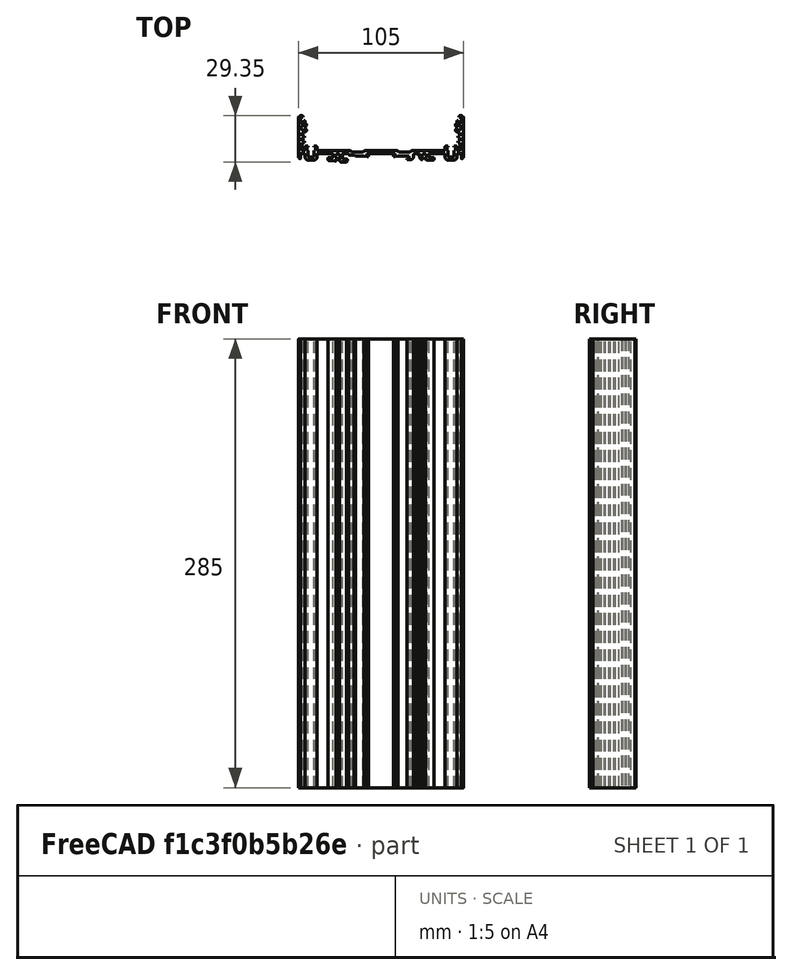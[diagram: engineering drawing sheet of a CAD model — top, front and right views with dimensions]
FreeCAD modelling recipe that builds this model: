
FCSTD DOCUMENT  (FreeCAD 0.20R29603 (Git))
Label: UM-ALU 4-100,5
License: All rights reserved
LicenseURL: http://en.wikipedia.org/wiki/All_rights_reserved
objects: Sketcher::SketchObject×1, PartDesign::Pad×1, PartDesign::Body×1
note: 4 computed .brp shape members not serialized (recipe doc carries the construction recipe); baked Part::Feature solids carry a one-line shape summary decoded from their .brp

FEATURE [Sketcher::SketchObject] Sketch
  FullyConstrained = false
  sketch-geometry (235):
    g0: LineSegment StartX=-40.7 StartY=5.3 StartZ=0 EndX=-40.7 EndY=4 EndZ=0
    g1: ArcOfCircle CenterX=-41.7 CenterY=5.3 CenterZ=0 NormalX=0 NormalY=0 NormalZ=1 AngleXU=1.5708 Radius=1 StartAngle=4.71239 EndAngle=6.28319
    g2: LineSegment StartX=-42.8 StartY=6.3 StartZ=0 EndX=-41.7 EndY=6.3 EndZ=0
    g3: LineSegment StartX=-42.8 StartY=5.6 StartZ=0 EndX=-42.8 EndY=6.3 EndZ=0
    g4: LineSegment StartX=-41.9 StartY=5.6 StartZ=0 EndX=-42.8 EndY=5.6 EndZ=0
    g5: LineSegment StartX=-41.9 StartY=3.4 StartZ=0 EndX=-41.9 EndY=5.6 EndZ=0
    g6: LineSegment StartX=-42.8 StartY=3.4 StartZ=0 EndX=-41.9 EndY=3.4 EndZ=0
    g7: LineSegment StartX=-42.8 StartY=-0.1 StartZ=0 EndX=-42.8 EndY=3.4 EndZ=0
    g8: ArcOfCircle CenterX=-43.3 CenterY=-0.1 CenterZ=0 NormalX=0 NormalY=0 NormalZ=1 AngleXU=1.5708 Radius=0.5 StartAngle=3.14159 EndAngle=4.71239
    g9: LineSegment StartX=-45.9 StartY=-0.6 StartZ=0 EndX=-43.3 EndY=-0.6 EndZ=0
    g10: ArcOfCircle CenterX=-45.9 CenterY=-0.1 CenterZ=0 NormalX=0 NormalY=0 NormalZ=1 AngleXU=1.5708 Radius=0.5 StartAngle=1.5708 EndAngle=3.14159
    g11: LineSegment StartX=-46.4 StartY=3.4 StartZ=0 EndX=-46.4 EndY=-0.1 EndZ=0
    g12: LineSegment StartX=-47.3 StartY=3.4 StartZ=0 EndX=-46.4 EndY=3.4 EndZ=0
    g13: LineSegment StartX=-47.3 StartY=5.6 StartZ=0 EndX=-47.3 EndY=3.4 EndZ=0
    g14: LineSegment StartX=-46.4 StartY=5.6 StartZ=0 EndX=-47.3 EndY=5.6 EndZ=0
    g15: LineSegment StartX=-46.4 StartY=6.3 StartZ=0 EndX=-46.4 EndY=5.6 EndZ=0
    g16: LineSegment StartX=-47.5 StartY=6.3 StartZ=0 EndX=-46.4 EndY=6.3 EndZ=0
    g17: ArcOfCircle CenterX=-47.5 CenterY=5.3 CenterZ=0 NormalX=0 NormalY=0 NormalZ=1 AngleXU=1.5708 Radius=1 StartAngle=0 EndAngle=1.5708
    g18: LineSegment StartX=-48.5 StartY=4 StartZ=0 EndX=-48.5 EndY=5.3 EndZ=0
    g19: ArcOfCircle CenterX=-49 CenterY=4 CenterZ=0 NormalX=0 NormalY=0 NormalZ=1 AngleXU=1.5708 Radius=0.5 StartAngle=3.14159 EndAngle=4.71239
    g20: LineSegment StartX=-50.1 StartY=3.5 StartZ=0 EndX=-49 EndY=3.5 EndZ=0
    g21: ArcOfCircle CenterX=-50.1 CenterY=3.8 CenterZ=0 NormalX=0 NormalY=0 NormalZ=1 AngleXU=1.5708 Radius=0.3 StartAngle=1.5708 EndAngle=3.14159
    g22: LineSegment StartX=-50.4 StartY=8.5 StartZ=0 EndX=-50.4 EndY=3.8 EndZ=0
    g23: LineSegment StartX=-48.9 StartY=8.5 StartZ=0 EndX=-50.4 EndY=8.5 EndZ=0
    g24: LineSegment StartX=-48.9 StartY=9.5 StartZ=0 EndX=-48.9 EndY=8.5 EndZ=0
    g25: LineSegment StartX=-50.4 StartY=9.5 StartZ=0 EndX=-48.9 EndY=9.5 EndZ=0
    g26: LineSegment StartX=-50.4 StartY=11.7 StartZ=0 EndX=-50.4 EndY=9.5 EndZ=0
    g27: LineSegment StartX=-48.9 StartY=11.7 StartZ=0 EndX=-50.4 EndY=11.7 EndZ=0
    g28: LineSegment StartX=-48.9 StartY=12.7 StartZ=0 EndX=-48.9 EndY=11.7 EndZ=0
    g29: LineSegment StartX=-50.4 StartY=12.7 StartZ=0 EndX=-48.9 EndY=12.7 EndZ=0
    g30: LineSegment StartX=-50.4 StartY=14.9 StartZ=0 EndX=-50.4 EndY=12.7 EndZ=0
    g31: LineSegment StartX=-49.65 StartY=14.9 StartZ=0 EndX=-50.4 EndY=14.9 EndZ=0
    g32: ArcOfCircle CenterX=-49.65 CenterY=17.9 CenterZ=0 NormalX=0 NormalY=0 NormalZ=1 AngleXU=1.5708 Radius=3 StartAngle=3.14159 EndAngle=3.97576
    g33: ArcOfCircle CenterX=-47.65 CenterY=16.0862 CenterZ=0 NormalX=0 NormalY=0 NormalZ=1 AngleXU=1.5708 Radius=0.3 StartAngle=3.97576 EndAngle=4.71239
    g34: LineSegment StartX=-47.35 StartY=16.3989 StartZ=0 EndX=-47.35 EndY=16.0862 EndZ=0
    g35: ArcOfCircle CenterX=-47.65 CenterY=16.3989 CenterZ=0 NormalX=0 NormalY=0 NormalZ=1 AngleXU=1.5708 Radius=0.3 StartAngle=4.71239 EndAngle=5.75959
    g36: LineSegment StartX=-48.2009 StartY=17.0633 StartZ=0 EndX=-47.5 EndY=16.6587 EndZ=0
    g37: ArcOfCircle CenterX=-48.3509 CenterY=16.8035 CenterZ=0 NormalX=0 NormalY=0 NormalZ=1 AngleXU=1.5708 Radius=0.3 StartAngle=5.75959 EndAngle=7.15298
    g38: ArcOfCircle CenterX=-49.65 CenterY=17.9 CenterZ=0 NormalX=0 NormalY=0 NormalZ=1 AngleXU=1.5708 Radius=1.4 StartAngle=5.41339 EndAngle=10.2946
    g39: ArcOfCircle CenterX=-48.3509 CenterY=18.9965 CenterZ=0 NormalX=0 NormalY=0 NormalZ=1 AngleXU=1.5708 Radius=0.3 StartAngle=2.27179 EndAngle=3.66519
    g40: LineSegment StartX=-47.5 StartY=19.1413 StartZ=0 EndX=-48.2009 EndY=18.7367 EndZ=0
    g41: ArcOfCircle CenterX=-47.65 CenterY=19.4011 CenterZ=0 NormalX=0 NormalY=0 NormalZ=1 AngleXU=1.5708 Radius=0.3 StartAngle=3.66519 EndAngle=4.71239
    g42: LineSegment StartX=-47.35 StartY=19.7138 StartZ=0 EndX=-47.35 EndY=19.4011 EndZ=0
    g43: ArcOfCircle CenterX=-47.65 CenterY=19.7138 CenterZ=0 NormalX=0 NormalY=0 NormalZ=1 AngleXU=1.5708 Radius=0.3 StartAngle=4.71239 EndAngle=5.44901
    g44: ArcOfCircle CenterX=-49.65 CenterY=17.9 CenterZ=0 NormalX=0 NormalY=0 NormalZ=1 AngleXU=1.5708 Radius=3 StartAngle=5.44901 EndAngle=5.777
    g45: ArcOfCircle CenterX=-48.05 CenterY=20.7862 CenterZ=0 NormalX=0 NormalY=0 NormalZ=1 AngleXU=1.5708 Radius=0.3 StartAngle=1.5708 EndAngle=2.6354
    g46: LineSegment StartX=-48.35 StartY=22 StartZ=0 EndX=-48.35 EndY=20.7862 EndZ=0
    g47: ArcOfCircle CenterX=-48.65 CenterY=22 CenterZ=0 NormalX=0 NormalY=0 NormalZ=1 AngleXU=1.5708 Radius=0.3 StartAngle=4.71239 EndAngle=6.28319
    g48: LineSegment StartX=-48.8851 StartY=22.3 StartZ=0 EndX=-48.65 EndY=22.3 EndZ=0
    g49: ArcOfCircle CenterX=-48.8851 CenterY=22 CenterZ=0 NormalX=0 NormalY=0 NormalZ=1 AngleXU=1.5708 Radius=0.3 StartAngle=0 EndAngle=1.80366
    g50: ArcOfCircle CenterX=-50.15 CenterY=21.7 CenterZ=0 NormalX=0 NormalY=0 NormalZ=1 AngleXU=1.5708 Radius=1 StartAngle=1.5708 EndAngle=4.94526
    g51: LineSegment StartX=-51.15 StartY=24.2 StartZ=0 EndX=-51.15 EndY=21.7 EndZ=0
    g52: ArcOfCircle CenterX=-50.85 CenterY=24.2 CenterZ=0 NormalX=0 NormalY=0 NormalZ=1 AngleXU=1.5708 Radius=0.3 StartAngle=0 EndAngle=1.5708
    g53: LineSegment StartX=-49.65 StartY=24.5 StartZ=0 EndX=-50.85 EndY=24.5 EndZ=0
    g54: LineSegment StartX=-49.65 StartY=25 StartZ=0 EndX=-49.65 EndY=24.5 EndZ=0
    g55: ArcOfCircle CenterX=-50.15 CenterY=25 CenterZ=0 NormalX=0 NormalY=0 NormalZ=1 AngleXU=1.5708 Radius=0.5 StartAngle=4.71239 EndAngle=6.28319
    g56: LineSegment StartX=-51.15 StartY=25.5 StartZ=0 EndX=-50.15 EndY=25.5 EndZ=0
    g57: ArcOfCircle CenterX=-51.15 CenterY=24.5 CenterZ=0 NormalX=0 NormalY=0 NormalZ=1 AngleXU=1.5708 Radius=1 StartAngle=0 EndAngle=1.09107
    g58: ArcOfCircle CenterX=-52.3033 CenterY=25.1 CenterZ=0 NormalX=0 NormalY=0 NormalZ=1 AngleXU=1.5708 Radius=0.3 StartAngle=3.14159 EndAngle=4.23266
    g59: LineSegment StartX=-52.35 StartY=24.8 StartZ=0 EndX=-52.3033 EndY=24.8 EndZ=0
    g60: ArcOfCircle CenterX=-52.35 CenterY=24.5 CenterZ=0 NormalX=0 NormalY=0 NormalZ=1 AngleXU=1.5708 Radius=0.3 StartAngle=0 EndAngle=1.5708
    g61: LineSegment StartX=-52.65 StartY=-0.205713 StartZ=0 EndX=-52.65 EndY=24.5 EndZ=0
    g62: ArcOfCircle CenterX=-50.85 CenterY=-0.205713 CenterZ=0 NormalX=0 NormalY=0 NormalZ=1 AngleXU=1.5708 Radius=1.8 StartAngle=1.5708 EndAngle=2.72258
    g63: LineSegment StartX=-51.45 StartY=-1.85 StartZ=0 EndX=-51.5823 EndY=-1.85 EndZ=0
    g64: ArcOfCircle CenterX=-51.45 CenterY=-1.55 CenterZ=0 NormalX=0 NormalY=0 NormalZ=1 AngleXU=1.5708 Radius=0.3 StartAngle=3.14159 EndAngle=4.71239
    g65: LineSegment StartX=-51.15 StartY=1.2 StartZ=0 EndX=-51.15 EndY=-1.55 EndZ=0
    g66: ArcOfCircle CenterX=-50.85 CenterY=1.2 CenterZ=0 NormalX=0 NormalY=0 NormalZ=1 AngleXU=1.5708 Radius=0.3 StartAngle=0 EndAngle=1.5708
    g67: LineSegment StartX=-48.9 StartY=1.5 StartZ=0 EndX=-50.85 EndY=1.5 EndZ=0
    g68: ArcOfCircle CenterX=-48.9 CenterY=1 CenterZ=0 NormalX=0 NormalY=0 NormalZ=1 AngleXU=1.5708 Radius=0.5 StartAngle=4.71239 EndAngle=6.28319
    g69: LineSegment StartX=-48.4 StartY=-0.6 StartZ=0 EndX=-48.4 EndY=1 EndZ=0
    g70: ArcOfCircle CenterX=-46.4 CenterY=-0.6 CenterZ=0 NormalX=0 NormalY=0 NormalZ=1 AngleXU=1.5708 Radius=2 StartAngle=1.5708 EndAngle=3.14159
    g71: LineSegment StartX=-42.8 StartY=-2.6 StartZ=0 EndX=-46.4 EndY=-2.6 EndZ=0
    g72: ArcOfCircle CenterX=-42.8 CenterY=-0.6 CenterZ=0 NormalX=0 NormalY=0 NormalZ=1 AngleXU=1.5708 Radius=2 StartAngle=3.14159 EndAngle=4.71239
    g73: LineSegment StartX=-40.8 StartY=1 StartZ=0 EndX=-40.8 EndY=-0.6 EndZ=0
    g74: ArcOfCircle CenterX=-40.3 CenterY=1 CenterZ=0 NormalX=0 NormalY=0 NormalZ=1 AngleXU=1.5708 Radius=0.5 StartAngle=0 EndAngle=1.5708
    g75: LineSegment StartX=-30.95 StartY=1.5 StartZ=0 EndX=-40.3 EndY=1.5 EndZ=0
    g76: ArcOfCircle CenterX=-30.95 CenterY=1.2 CenterZ=0 NormalX=0 NormalY=0 NormalZ=1 AngleXU=1.5708 Radius=0.3 StartAngle=4.71239 EndAngle=6.28319
    g77: LineSegment StartX=-30.65 StartY=-0.85 StartZ=0 EndX=-30.65 EndY=1.2 EndZ=0
    g78: ArcOfCircle CenterX=-30.95 CenterY=-0.85 CenterZ=0 NormalX=0 NormalY=0 NormalZ=1 AngleXU=1.5708 Radius=0.3 StartAngle=3.14159 EndAngle=4.71239
    g79: LineSegment StartX=-33.55 StartY=-1.15 StartZ=0 EndX=-30.95 EndY=-1.15 EndZ=0
    g80: ArcOfCircle CenterX=-33.55 CenterY=-1.45 CenterZ=0 NormalX=0 NormalY=0 NormalZ=1 AngleXU=1.5708 Radius=0.3 StartAngle=0 EndAngle=1.5708
    g81: LineSegment StartX=-33.85 StartY=-2.37492 StartZ=0 EndX=-33.85 EndY=-1.45 EndZ=0
    g82: ArcOfCircle CenterX=-33.35 CenterY=-2.37492 CenterZ=0 NormalX=0 NormalY=0 NormalZ=1 AngleXU=1.5708 Radius=0.5 StartAngle=1.5708 EndAngle=3.01069
    g83: LineSegment StartX=-29.3653 StartY=-3.40384 StartZ=0 EndX=-33.4153 EndY=-2.87064 EndZ=0
    g84: ArcOfCircle CenterX=-29.3 CenterY=-2.90811 CenterZ=0 NormalX=0 NormalY=0 NormalZ=1 AngleXU=1.5708 Radius=0.5 StartAngle=3.01069 EndAngle=4.71239
    g85: LineSegment StartX=-28.8 StartY=-2.09186 StartZ=0 EndX=-28.8 EndY=-2.90811 EndZ=0
    g86: LineSegment StartX=-28.4867 StartY=-1.54914 StartZ=0 EndX=-28.8 EndY=-2.09186 EndZ=0
    g87: ArcOfCircle CenterX=-28.7465 CenterY=-1.39914 CenterZ=0 NormalX=0 NormalY=0 NormalZ=1 AngleXU=1.5708 Radius=0.3 StartAngle=4.18879 EndAngle=5.58219
    g88: ArcOfCircle CenterX=-27.65 CenterY=-0.1 CenterZ=0 NormalX=0 NormalY=0 NormalZ=1 AngleXU=1.5708 Radius=1.4 StartAngle=3.84259 EndAngle=8.72378
    g89: ArcOfCircle CenterX=-26.5535 CenterY=-1.39914 CenterZ=0 NormalX=0 NormalY=0 NormalZ=1 AngleXU=1.5708 Radius=0.3 StartAngle=0.700998 EndAngle=2.0944
    g90: LineSegment StartX=-26.5 StartY=-2.09186 StartZ=0 EndX=-26.8133 EndY=-1.54914 EndZ=0
    g91: LineSegment StartX=-26.5 StartY=-2.85 StartZ=0 EndX=-26.5 EndY=-2.09186 EndZ=0
    g92: ArcOfCircle CenterX=-25.5 CenterY=-2.85 CenterZ=0 NormalX=0 NormalY=0 NormalZ=1 AngleXU=1.5708 Radius=1 StartAngle=1.5708 EndAngle=3.14159
    g93: LineSegment StartX=-22.0274 StartY=-3.85 StartZ=0 EndX=-25.5 EndY=-3.85 EndZ=0
    g94: LineSegment StartX=-21.45 StartY=-2.85 StartZ=0 EndX=-22.0274 EndY=-3.85 EndZ=0
    g95: LineSegment StartX=-21.45 StartY=-2.45 StartZ=0 EndX=-21.45 EndY=-2.85 EndZ=0
    g96: ArcOfCircle CenterX=-21.75 CenterY=-2.45 CenterZ=0 NormalX=0 NormalY=0 NormalZ=1 AngleXU=1.5708 Radius=0.3 StartAngle=4.71239 EndAngle=6.28319
    g97: LineSegment StartX=-24.35 StartY=-2.15 StartZ=0 EndX=-21.75 EndY=-2.15 EndZ=0
    g98: ArcOfCircle CenterX=-24.35 CenterY=-1.85 CenterZ=0 NormalX=0 NormalY=0 NormalZ=1 AngleXU=1.5708 Radius=0.3 StartAngle=1.5708 EndAngle=3.14159
    g99: LineSegment StartX=-24.65 StartY=1.2 StartZ=0 EndX=-24.65 EndY=-1.85 EndZ=0
    g100: ArcOfCircle CenterX=-24.35 CenterY=1.2 CenterZ=0 NormalX=0 NormalY=0 NormalZ=1 AngleXU=1.5708 Radius=0.3 StartAngle=0 EndAngle=1.5708
    g101: LineSegment StartX=-20.95 StartY=1.5 StartZ=0 EndX=-24.35 EndY=1.5 EndZ=0
    g102: ArcOfCircle CenterX=-20.95 CenterY=1.2 CenterZ=0 NormalX=0 NormalY=0 NormalZ=1 AngleXU=1.5708 Radius=0.3 StartAngle=4.71239 EndAngle=6.28319
    g103: LineSegment StartX=-20.65 StartY=0.8 StartZ=0 EndX=-20.65 EndY=1.2 EndZ=0
    g104: ArcOfCircle CenterX=-20.35 CenterY=0.8 CenterZ=0 NormalX=0 NormalY=0 NormalZ=1 AngleXU=1.5708 Radius=0.3 StartAngle=1.5708 EndAngle=3.14159
    g105: LineSegment StartX=-17.216 StartY=0.5 StartZ=0 EndX=-20.35 EndY=0.5 EndZ=0
    g106: LineSegment StartX=-16.35 StartY=3.6e-15 StartZ=0 EndX=-17.216 EndY=0.5 EndZ=0
    g107: LineSegment StartX=-11.016 StartY=1.8e-15 StartZ=0 EndX=-16.35 EndY=3e-15 EndZ=0
    g108: LineSegment StartX=-9.15 StartY=-0.5 StartZ=0 EndX=-11.016 EndY=-3.13e-14 EndZ=0
    g109: LineSegment StartX=-8.15 StartY=-0.5 StartZ=0 EndX=-9.15 EndY=-0.5 EndZ=0
    g110: LineSegment StartX=-8.15 StartY=0.5 StartZ=0 EndX=-8.15 EndY=-0.5 EndZ=0
    g111: LineSegment StartX=-9.15 StartY=0.5 StartZ=0 EndX=-8.15 EndY=0.5 EndZ=0
    g112: LineSegment StartX=-9.15 StartY=1.5 StartZ=0 EndX=-9.15 EndY=0.5 EndZ=0
    g113: LineSegment StartX=8.85 StartY=1.5 StartZ=0 EndX=-9.15 EndY=1.5 EndZ=0
    g114: LineSegment StartX=8.85 StartY=0.5 StartZ=0 EndX=8.85 EndY=1.5 EndZ=0
    g115: LineSegment StartX=7.85 StartY=0.5 StartZ=0 EndX=8.85 EndY=0.5 EndZ=0
    g116: LineSegment StartX=7.85 StartY=-0.5 StartZ=0 EndX=7.85 EndY=0.5 EndZ=0
    g117: LineSegment StartX=8.85 StartY=-0.5 StartZ=0 EndX=7.85 EndY=-0.5 EndZ=0
    g118: LineSegment StartX=10.716 StartY=-1.8e-15 StartZ=0 EndX=8.85 EndY=-0.5 EndZ=0
    g119: LineSegment StartX=17.5 StartY=-3.6e-15 StartZ=0 EndX=10.716 EndY=-2e-15 EndZ=0
    g120: LineSegment StartX=17.5 StartY=-1.1 StartZ=0 EndX=17.5 EndY=-3.6e-15 EndZ=0
    g121: LineSegment StartX=16.3 StartY=-1.59706 StartZ=0 EndX=17.5 EndY=-1.1 EndZ=0
    g122: LineSegment StartX=16.3 StartY=-2.4 StartZ=0 EndX=16.3 EndY=-1.59706 EndZ=0
    g123: LineSegment StartX=18.5 StartY=-2.4 StartZ=0 EndX=16.3 EndY=-2.4 EndZ=0
    g124: ArcOfCircle CenterX=18.5 CenterY=-0.4 CenterZ=0 NormalX=0 NormalY=0 NormalZ=1 AngleXU=1.5708 Radius=2 StartAngle=3.14159 EndAngle=4.71239
    g125: LineSegment StartX=20.5 StartY=0.5 StartZ=0 EndX=20.5 EndY=-0.4 EndZ=0
    g126: ArcOfCircle CenterX=21.5 CenterY=0.5 CenterZ=0 NormalX=0 NormalY=0 NormalZ=1 AngleXU=1.5708 Radius=1 StartAngle=0 EndAngle=1.5708
    g127: LineSegment StartX=22.475 StartY=1.5 StartZ=0 EndX=21.5 EndY=1.5 EndZ=0
    g128: ArcOfCircle CenterX=22.775 CenterY=1.5 CenterZ=0 NormalX=0 NormalY=0 NormalZ=1 AngleXU=1.5708 Radius=0.3 StartAngle=1.5708 EndAngle=4.71239
    g129: LineSegment StartX=24.05 StartY=1.5 StartZ=0 EndX=23.075 EndY=1.5 EndZ=0
    g130: ArcOfCircle CenterX=24.05 CenterY=1.2 CenterZ=0 NormalX=0 NormalY=0 NormalZ=1 AngleXU=1.5708 Radius=0.3 StartAngle=4.71239 EndAngle=6.28319
    g131: LineSegment StartX=24.35 StartY=-0.1 StartZ=0 EndX=24.35 EndY=1.2 EndZ=0
    g132: ArcOfCircle CenterX=27.35 CenterY=-0.1 CenterZ=0 NormalX=0 NormalY=0 NormalZ=1 AngleXU=1.5708 Radius=3 StartAngle=1.5708 EndAngle=2.41664
    g133: ArcOfCircle CenterX=25.6922 CenterY=-1.97132 CenterZ=0 NormalX=0 NormalY=0 NormalZ=1 AngleXU=1.5708 Radius=0.5 StartAngle=2.41664 EndAngle=4.18879
    g134: LineSegment StartX=26.5133 StartY=-1.54914 StartZ=0 EndX=26.1253 EndY=-2.22132 EndZ=0
    g135: ArcOfCircle CenterX=26.2535 CenterY=-1.39914 CenterZ=0 NormalX=0 NormalY=0 NormalZ=1 AngleXU=1.5708 Radius=0.3 StartAngle=4.18879 EndAngle=5.58219
    g136: ArcOfCircle CenterX=27.35 CenterY=-0.1 CenterZ=0 NormalX=0 NormalY=0 NormalZ=1 AngleXU=1.5708 Radius=1.4 StartAngle=3.84259 EndAngle=8.72378
    g137: ArcOfCircle CenterX=28.4465 CenterY=-1.39914 CenterZ=0 NormalX=0 NormalY=0 NormalZ=1 AngleXU=1.5708 Radius=0.3 StartAngle=0.700998 EndAngle=2.0944
    g138: LineSegment StartX=28.7356 StartY=-2.5 StartZ=0 EndX=28.1867 EndY=-1.54914 EndZ=0
    g139: ArcOfCircle CenterX=28.9954 CenterY=-2.35 CenterZ=0 NormalX=0 NormalY=0 NormalZ=1 AngleXU=1.5708 Radius=0.3 StartAngle=2.0944 EndAngle=3.14159
    g140: LineSegment StartX=33.25 StartY=-2.65 StartZ=0 EndX=28.9954 EndY=-2.65 EndZ=0
    g141: ArcOfCircle CenterX=33.25 CenterY=-2.35 CenterZ=0 NormalX=0 NormalY=0 NormalZ=1 AngleXU=1.5708 Radius=0.3 StartAngle=3.14159 EndAngle=4.71239
    g142: LineSegment StartX=33.55 StartY=-1.45 StartZ=0 EndX=33.55 EndY=-2.35 EndZ=0
    g143: ArcOfCircle CenterX=33.25 CenterY=-1.45 CenterZ=0 NormalX=0 NormalY=0 NormalZ=1 AngleXU=1.5708 Radius=0.3 StartAngle=4.71239 EndAngle=6.28319
    g144: LineSegment StartX=30.65 StartY=-1.15 StartZ=0 EndX=33.25 EndY=-1.15 EndZ=0
    g145: ArcOfCircle CenterX=30.65 CenterY=-0.85 CenterZ=0 NormalX=0 NormalY=0 NormalZ=1 AngleXU=1.5708 Radius=0.3 StartAngle=1.5708 EndAngle=3.14159
    g146: LineSegment StartX=30.35 StartY=1.2 StartZ=0 EndX=30.35 EndY=-0.85 EndZ=0
    g147: ArcOfCircle CenterX=30.65 CenterY=1.2 CenterZ=0 NormalX=0 NormalY=0 NormalZ=1 AngleXU=1.5708 Radius=0.3 StartAngle=0 EndAngle=1.5708
    g148: LineSegment StartX=40 StartY=1.5 StartZ=0 EndX=30.65 EndY=1.5 EndZ=0
    g149: ArcOfCircle CenterX=40 CenterY=1 CenterZ=0 NormalX=0 NormalY=0 NormalZ=1 AngleXU=1.5708 Radius=0.5 StartAngle=4.71239 EndAngle=6.28319
    g150: LineSegment StartX=40.5 StartY=-0.6 StartZ=0 EndX=40.5 EndY=1 EndZ=0
    g151: ArcOfCircle CenterX=42.5 CenterY=-0.6 CenterZ=0 NormalX=0 NormalY=0 NormalZ=1 AngleXU=1.5708 Radius=2 StartAngle=1.5708 EndAngle=3.14159
    g152: LineSegment StartX=46.1 StartY=-2.6 StartZ=0 EndX=42.5 EndY=-2.6 EndZ=0
    g153: ArcOfCircle CenterX=46.1 CenterY=-0.6 CenterZ=0 NormalX=0 NormalY=0 NormalZ=1 AngleXU=1.5708 Radius=2 StartAngle=3.14159 EndAngle=4.71239
    g154: LineSegment StartX=48.1 StartY=1 StartZ=0 EndX=48.1 EndY=-0.6 EndZ=0
    g155: ArcOfCircle CenterX=48.6 CenterY=1 CenterZ=0 NormalX=0 NormalY=0 NormalZ=1 AngleXU=1.5708 Radius=0.5 StartAngle=0 EndAngle=1.5708
    g156: LineSegment StartX=50.55 StartY=1.5 StartZ=0 EndX=48.6 EndY=1.5 EndZ=0
    g157: ArcOfCircle CenterX=50.55 CenterY=1.2 CenterZ=0 NormalX=0 NormalY=0 NormalZ=1 AngleXU=1.5708 Radius=0.3 StartAngle=4.71239 EndAngle=6.28319
    g158: LineSegment StartX=50.85 StartY=-1.55 StartZ=0 EndX=50.85 EndY=1.2 EndZ=0
    g159: ArcOfCircle CenterX=51.15 CenterY=-1.55 CenterZ=0 NormalX=0 NormalY=0 NormalZ=1 AngleXU=1.5708 Radius=0.3 StartAngle=1.5708 EndAngle=3.14159
    g160: LineSegment StartX=51.2823 StartY=-1.85 StartZ=0 EndX=51.15 EndY=-1.85 EndZ=0
    g161: ArcOfCircle CenterX=50.55 CenterY=-0.205713 CenterZ=0 NormalX=0 NormalY=0 NormalZ=1 AngleXU=1.5708 Radius=1.8 StartAngle=3.5606 EndAngle=4.71239
    g162: LineSegment StartX=52.35 StartY=24.5 StartZ=0 EndX=52.35 EndY=-0.205713 EndZ=0
    g163: ArcOfCircle CenterX=52.05 CenterY=24.5 CenterZ=0 NormalX=0 NormalY=0 NormalZ=1 AngleXU=1.5708 Radius=0.3 StartAngle=4.71239 EndAngle=6.28319
    g164: LineSegment StartX=52.0033 StartY=24.8 StartZ=0 EndX=52.05 EndY=24.8 EndZ=0
    g165: ArcOfCircle CenterX=52.0033 CenterY=25.1 CenterZ=0 NormalX=0 NormalY=0 NormalZ=1 AngleXU=1.5708 Radius=0.3 StartAngle=2.05052 EndAngle=3.14159
    g166: ArcOfCircle CenterX=50.85 CenterY=24.5 CenterZ=0 NormalX=0 NormalY=0 NormalZ=1 AngleXU=1.5708 Radius=1 StartAngle=5.19212 EndAngle=6.28319
    g167: LineSegment StartX=49.85 StartY=25.5 StartZ=0 EndX=50.85 EndY=25.5 EndZ=0
    g168: ArcOfCircle CenterX=49.85 CenterY=25 CenterZ=0 NormalX=0 NormalY=0 NormalZ=1 AngleXU=1.5708 Radius=0.5 StartAngle=0 EndAngle=1.5708
    g169: LineSegment StartX=49.35 StartY=24.5 StartZ=0 EndX=49.35 EndY=25 EndZ=0
    g170: LineSegment StartX=50.55 StartY=24.5 StartZ=0 EndX=49.35 EndY=24.5 EndZ=0
    g171: ArcOfCircle CenterX=50.55 CenterY=24.2 CenterZ=0 NormalX=0 NormalY=0 NormalZ=1 AngleXU=1.5708 Radius=0.3 StartAngle=4.71239 EndAngle=6.28319
    g172: LineSegment StartX=50.85 StartY=21.7 StartZ=0 EndX=50.85 EndY=24.2 EndZ=0
    g173: ArcOfCircle CenterX=49.85 CenterY=21.7 CenterZ=0 NormalX=0 NormalY=0 NormalZ=1 AngleXU=1.5708 Radius=1 StartAngle=1.33793 EndAngle=4.71239
    g174: ArcOfCircle CenterX=48.5851 CenterY=22 CenterZ=0 NormalX=0 NormalY=0 NormalZ=1 AngleXU=1.5708 Radius=0.3 StartAngle=4.47952 EndAngle=6.28319
    g175: LineSegment StartX=48.35 StartY=22.3 StartZ=0 EndX=48.5851 EndY=22.3 EndZ=0
    g176: ArcOfCircle CenterX=48.35 CenterY=22 CenterZ=0 NormalX=0 NormalY=0 NormalZ=1 AngleXU=1.5708 Radius=0.3 StartAngle=0 EndAngle=1.5708
    g177: LineSegment StartX=48.05 StartY=20.7862 StartZ=0 EndX=48.05 EndY=22 EndZ=0
    g178: ArcOfCircle CenterX=47.75 CenterY=20.7862 CenterZ=0 NormalX=0 NormalY=0 NormalZ=1 AngleXU=1.5708 Radius=0.3 StartAngle=3.64778 EndAngle=4.71239
    g179: ArcOfCircle CenterX=49.35 CenterY=17.9 CenterZ=0 NormalX=0 NormalY=0 NormalZ=1 AngleXU=1.5708 Radius=3 StartAngle=0.50619 EndAngle=0.834172
    g180: ArcOfCircle CenterX=47.35 CenterY=19.7138 CenterZ=0 NormalX=0 NormalY=0 NormalZ=1 AngleXU=1.5708 Radius=0.3 StartAngle=0.834172 EndAngle=1.5708
    g181: LineSegment StartX=47.05 StartY=19.4011 StartZ=0 EndX=47.05 EndY=19.7138 EndZ=0
    g182: ArcOfCircle CenterX=47.35 CenterY=19.4011 CenterZ=0 NormalX=0 NormalY=0 NormalZ=1 AngleXU=1.5708 Radius=0.3 StartAngle=1.5708 EndAngle=2.61799
    g183: LineSegment StartX=47.9009 StartY=18.7367 StartZ=0 EndX=47.2 EndY=19.1413 EndZ=0
    g184: ArcOfCircle CenterX=48.0509 CenterY=18.9965 CenterZ=0 NormalX=0 NormalY=0 NormalZ=1 AngleXU=1.5708 Radius=0.3 StartAngle=2.61799 EndAngle=4.01139
    g185: ArcOfCircle CenterX=49.35 CenterY=17.9 CenterZ=0 NormalX=0 NormalY=0 NormalZ=1 AngleXU=1.5708 Radius=1.4 StartAngle=2.27179 EndAngle=7.15298
    g186: ArcOfCircle CenterX=48.0509 CenterY=16.8035 CenterZ=0 NormalX=0 NormalY=0 NormalZ=1 AngleXU=1.5708 Radius=0.3 StartAngle=5.41339 EndAngle=6.80678
    g187: LineSegment StartX=47.2 StartY=16.6587 StartZ=0 EndX=47.9009 EndY=17.0633 EndZ=0
    g188: ArcOfCircle CenterX=47.35 CenterY=16.3989 CenterZ=0 NormalX=0 NormalY=0 NormalZ=1 AngleXU=1.5708 Radius=0.3 StartAngle=0.523599 EndAngle=1.5708
    g189: LineSegment StartX=47.05 StartY=16.0862 StartZ=0 EndX=47.05 EndY=16.3989 EndZ=0
    g190: ArcOfCircle CenterX=47.35 CenterY=16.0862 CenterZ=0 NormalX=0 NormalY=0 NormalZ=1 AngleXU=1.5708 Radius=0.3 StartAngle=1.5708 EndAngle=2.30742
    g191: ArcOfCircle CenterX=49.35 CenterY=17.9 CenterZ=0 NormalX=0 NormalY=0 NormalZ=1 AngleXU=1.5708 Radius=3 StartAngle=2.30742 EndAngle=3.14159
    g192: LineSegment StartX=50.1 StartY=14.9 StartZ=0 EndX=49.35 EndY=14.9 EndZ=0
    g193: LineSegment StartX=50.1 StartY=12.7 StartZ=0 EndX=50.1 EndY=14.9 EndZ=0
    g194: LineSegment StartX=48.6 StartY=12.7 StartZ=0 EndX=50.1 EndY=12.7 EndZ=0
    g195: LineSegment StartX=48.6 StartY=11.7 StartZ=0 EndX=48.6 EndY=12.7 EndZ=0
    g196: LineSegment StartX=50.1 StartY=11.7 StartZ=0 EndX=48.6 EndY=11.7 EndZ=0
    g197: LineSegment StartX=50.1 StartY=9.5 StartZ=0 EndX=50.1 EndY=11.7 EndZ=0
    g198: LineSegment StartX=48.6 StartY=9.5 StartZ=0 EndX=50.1 EndY=9.5 EndZ=0
    g199: LineSegment StartX=48.6 StartY=8.5 StartZ=0 EndX=48.6 EndY=9.5 EndZ=0
    g200: LineSegment StartX=50.1 StartY=8.5 StartZ=0 EndX=48.6 EndY=8.5 EndZ=0
    g201: LineSegment StartX=50.1 StartY=3.8 StartZ=0 EndX=50.1 EndY=8.5 EndZ=0
    g202: ArcOfCircle CenterX=49.8 CenterY=3.8 CenterZ=0 NormalX=0 NormalY=0 NormalZ=1 AngleXU=1.5708 Radius=0.3 StartAngle=3.14159 EndAngle=4.71239
    g203: LineSegment StartX=48.7 StartY=3.5 StartZ=0 EndX=49.8 EndY=3.5 EndZ=0
    g204: ArcOfCircle CenterX=48.7 CenterY=4 CenterZ=0 NormalX=0 NormalY=0 NormalZ=1 AngleXU=1.5708 Radius=0.5 StartAngle=1.5708 EndAngle=3.14159
    g205: LineSegment StartX=48.2 StartY=5.3 StartZ=0 EndX=48.2 EndY=4 EndZ=0
    g206: ArcOfCircle CenterX=47.2 CenterY=5.3 CenterZ=0 NormalX=0 NormalY=0 NormalZ=1 AngleXU=1.5708 Radius=1 StartAngle=4.71239 EndAngle=6.28319
    g207: LineSegment StartX=46.1 StartY=6.3 StartZ=0 EndX=47.2 EndY=6.3 EndZ=0
    g208: LineSegment StartX=46.1 StartY=5.6 StartZ=0 EndX=46.1 EndY=6.3 EndZ=0
    g209: LineSegment StartX=47 StartY=5.6 StartZ=0 EndX=46.1 EndY=5.6 EndZ=0
    g210: LineSegment StartX=47 StartY=3.4 StartZ=0 EndX=47 EndY=5.6 EndZ=0
    g211: LineSegment StartX=46.1 StartY=3.4 StartZ=0 EndX=47 EndY=3.4 EndZ=0
    g212: LineSegment StartX=46.1 StartY=-0.1 StartZ=0 EndX=46.1 EndY=3.4 EndZ=0
    g213: ArcOfCircle CenterX=45.6 CenterY=-0.1 CenterZ=0 NormalX=0 NormalY=0 NormalZ=1 AngleXU=1.5708 Radius=0.5 StartAngle=3.14159 EndAngle=4.71239
    g214: LineSegment StartX=43 StartY=-0.6 StartZ=0 EndX=45.6 EndY=-0.6 EndZ=0
    g215: ArcOfCircle CenterX=43 CenterY=-0.1 CenterZ=0 NormalX=0 NormalY=0 NormalZ=1 AngleXU=1.5708 Radius=0.5 StartAngle=1.5708 EndAngle=3.14159
    g216: LineSegment StartX=42.5 StartY=3.4 StartZ=0 EndX=42.5 EndY=-0.1 EndZ=0
    g217: LineSegment StartX=41.6 StartY=3.4 StartZ=0 EndX=42.5 EndY=3.4 EndZ=0
    g218: LineSegment StartX=41.6 StartY=5.6 StartZ=0 EndX=41.6 EndY=3.4 EndZ=0
    g219: LineSegment StartX=42.5 StartY=5.6 StartZ=0 EndX=41.6 EndY=5.6 EndZ=0
    g220: LineSegment StartX=42.5 StartY=6.3 StartZ=0 EndX=42.5 EndY=5.6 EndZ=0
    g221: LineSegment StartX=41.4 StartY=6.3 StartZ=0 EndX=42.5 EndY=6.3 EndZ=0
    g222: ArcOfCircle CenterX=41.4 CenterY=5.3 CenterZ=0 NormalX=0 NormalY=0 NormalZ=1 AngleXU=1.5708 Radius=1 StartAngle=0 EndAngle=1.5708
    g223: LineSegment StartX=40.4 StartY=4 StartZ=0 EndX=40.4 EndY=5.3 EndZ=0
    g224: ArcOfCircle CenterX=39.9 CenterY=4 CenterZ=0 NormalX=0 NormalY=0 NormalZ=1 AngleXU=1.5708 Radius=0.5 StartAngle=3.14159 EndAngle=4.71239
    g225: LineSegment StartX=19.35 StartY=3.5 StartZ=0 EndX=39.9 EndY=3.5 EndZ=0
    g226: LineSegment StartX=18.35 StartY=2.5 StartZ=0 EndX=19.35 EndY=3.5 EndZ=0
    g227: LineSegment StartX=11.35 StartY=2.5 StartZ=0 EndX=18.35 EndY=2.5 EndZ=0
    g228: LineSegment StartX=10.35 StartY=3.5 StartZ=0 EndX=11.35 EndY=2.5 EndZ=0
    g229: LineSegment StartX=-10.65 StartY=3.5 StartZ=0 EndX=10.35 EndY=3.5 EndZ=0
    g230: LineSegment StartX=-11.65 StartY=2.5 StartZ=0 EndX=-10.65 EndY=3.5 EndZ=0
    g231: LineSegment StartX=-18.65 StartY=2.5 StartZ=0 EndX=-11.65 EndY=2.5 EndZ=0
    g232: LineSegment StartX=-19.65 StartY=3.5 StartZ=0 EndX=-18.65 EndY=2.5 EndZ=0
    g233: LineSegment StartX=-40.2 StartY=3.5 StartZ=0 EndX=-19.65 EndY=3.5 EndZ=0
    g234: ArcOfCircle CenterX=-40.2 CenterY=4 CenterZ=0 NormalX=0 NormalY=0 NormalZ=1 AngleXU=1.5708 Radius=0.5 StartAngle=1.5708 EndAngle=3.14159
FEATURE [PartDesign::Pad] Pad
  Direction = (0,0,1)
  Length = 285
  Length2 = 10
  Profile = -> Sketch
  ReferenceAxis = -> Sketch [N_Axis]
  Type = 0
FEATURE [PartDesign::Body] Body
  Group = -> [Sketch,Pad]
  Origin = -> Origin
  Tip = -> Pad
